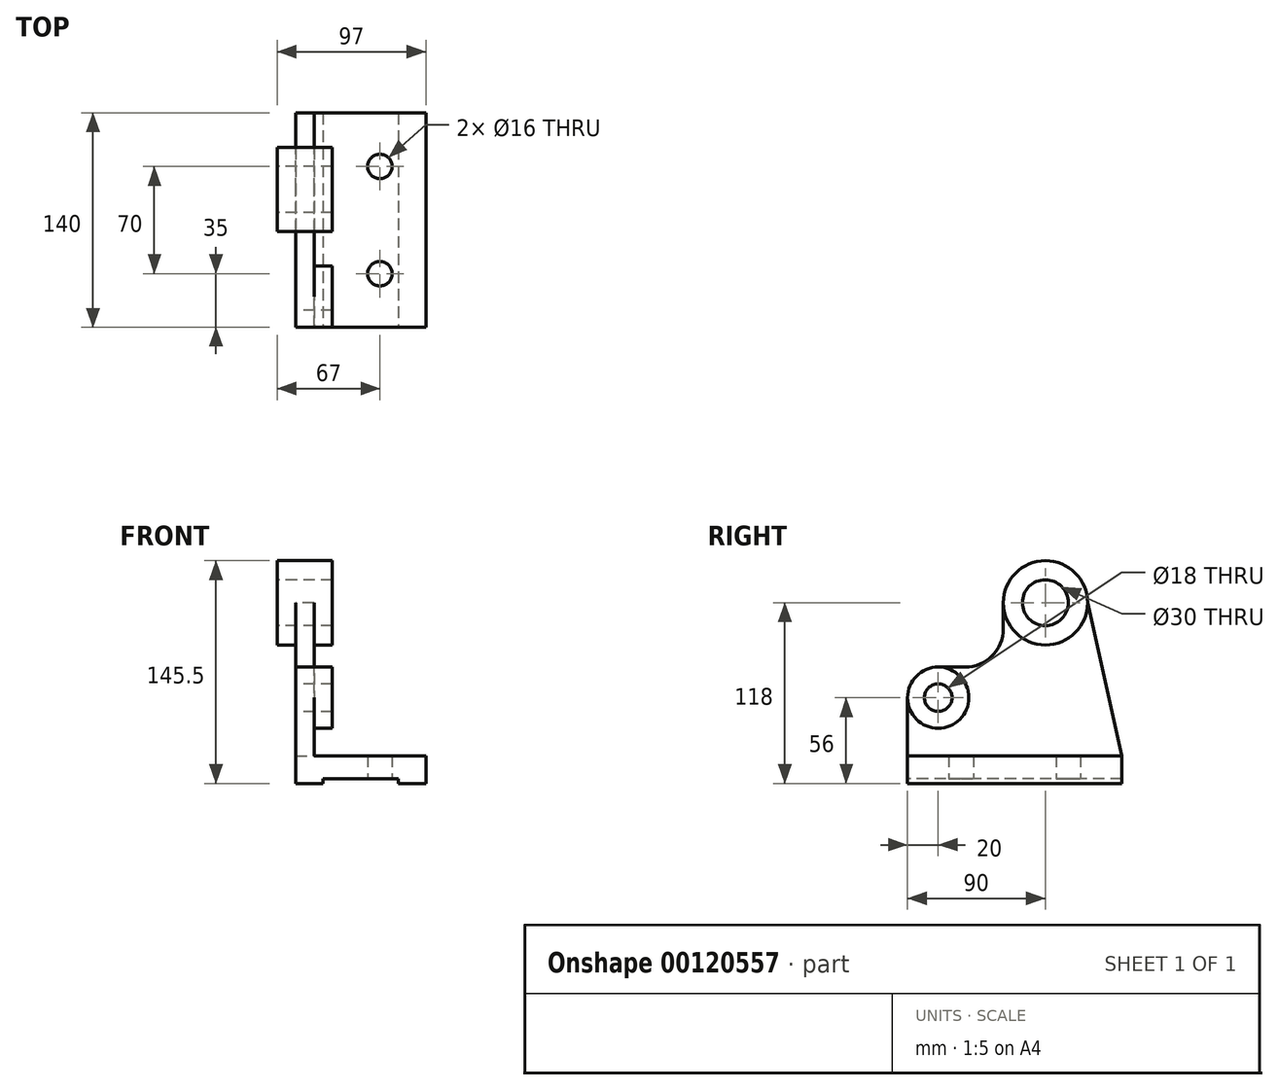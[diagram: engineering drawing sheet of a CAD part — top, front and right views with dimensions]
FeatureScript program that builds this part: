
annotation { "Feature Type Name" : "Feature", "Feature Type Description" : "" }
export const myFeature = defineFeature(function(context is Context, id is Id, definition is map)
    precondition{}
    {
        {
            var Q0;
            Q0=qCreatedBy(makeId("Top.planeOp"),FACE);
            var sketch = newSketch(context, id + "F0", { "sketchPlane" : qUnion([Q0])});
            skLineSegment(sketch, "E0.bottom", {"start": v(0, 70) * mm, "end": v(85, 70) * mm});
            skLineSegment(sketch, "E0.top", {"start": v(0, -70) * mm, "end": v(85, -70) * mm});
            skLineSegment(sketch, "E0.left", {"start": v(0, 70) * mm, "end": v(0, -70) * mm});
            skLineSegment(sketch, "E0.right", {"start": v(85, 70) * mm, "end": v(85, -70) * mm});
            skCircle(sketch, "E1", {"center": v(55, -35) * mm, "radius": 8 * mm});
            skCircle(sketch, "E2.MirrorC", {"center": v(55, 35) * mm, "radius": 8 * mm});
            skSolve(sketch);
        }
        {
            var Q0;
            Q0 = qSketchRegion(id + "F0", true);
            var Q1;
            Q1=makeQuery(id+"F0.imprint","IMPRINT",FACE,{"disambiguationData":[TD([[makeQuery(id+"F0.imprint","IMPRINT",EDGE,{"derivedFrom":sQuery(id+"F0.wireOp",EDGE,"E0.bottom")}),-1.0]])]});
            extrude(context, id + "F1", {"entities" : qUnion([Q0, Q1]), "depth" : 18 * mm});
        }
        {
            var Q0;
            Q0=makeQuery(id+"F1.opExtrude","SWEPT_FACE",FACE,{"disambiguationData":[OSD([sQuery(id+"F0.wireOp",EDGE,"E0.top")])]});
            var sketch = newSketch(context, id + "F2", { "sketchPlane" : qUnion([Q0])});
            skLineSegment(sketch, "E3", {"start": v(0, 0) * mm, "end": v(18, 0) * mm});
            skLineSegment(sketch, "E4", {"start": v(18, 0) * mm, "end": v(18, 3) * mm});
            skLineSegment(sketch, "E5", {"start": v(18, 3) * mm, "end": v(67, 3) * mm});
            skLineSegment(sketch, "E6", {"start": v(67, 3) * mm, "end": v(67, 0) * mm});
            skLineSegment(sketch, "E7", {"start": v(67, 0) * mm, "end": v(85, 0) * mm});
            skSolve(sketch);
        }
        {
            var Q0;
            Q0 = qSketchRegion(id + "F2", true);
            var Q1;
            {var subQ0=sQuery(id+"F2.wireOp",EDGE,"E4");Q1=makeQuery(id+"F2.imprint","IMPRINT",FACE,{"disambiguationData":[TD([[makeQuery(id+"F2.imprint","IMPRINT",EDGE,{"derivedFrom":subQ0}),-1.0]])]});}
            extrude(context, id + "F3", {"entities" : qUnion([Q0, Q1]), "operationType" : NewBodyOperationType.REMOVE, "endBound" : BoundingType.THROUGH_ALL, "oppositeDirection" : true, "depth" : 25 * mm});
        }
        {
            var Q0;
            Q0=makeQuery(id+"F1.opExtrude","CAP_FACE",FACE,{"disambiguationData":[OSD([sQuery(id+"F0.wireOp",EDGE,"E0.bottom"),sQuery(id+"F0.wireOp",EDGE,"E0.top"),sQuery(id+"F0.wireOp",EDGE,"E0.left"),sQuery(id+"F0.wireOp",EDGE,"E0.right")])],"isStart":false});
            var sketch = newSketch(context, id + "F4", { "sketchPlane" : qUnion([Q0])});
            skLineSegment(sketch, "E8.bottom", {"start": v(0, 70) * mm, "end": v(12, 70) * mm});
            skLineSegment(sketch, "E8.top", {"start": v(0, -70) * mm, "end": v(12, -70) * mm});
            skLineSegment(sketch, "E8.left", {"start": v(0, 70) * mm, "end": v(0, -70) * mm});
            skLineSegment(sketch, "E8.right", {"start": v(12, 70) * mm, "end": v(12, -70) * mm});
            skSolve(sketch);
        }
        {
            var Q0;
            Q0=makeQuery(id+"F4.imprint","IMPRINT",FACE,{"disambiguationData":[TD([[makeQuery(id+"F4.imprint","IMPRINT",EDGE,{"derivedFrom":sQuery(id+"F4.wireOp",EDGE,"E8.bottom")}),-1.0]])]});
            extrude(context, id + "F5", {"entities" : qUnion([Q0]), "operationType" : NewBodyOperationType.ADD, "depth" : 100 * mm});
        }
        {
            var Q0;
            Q0=makeQuery(id+"F5.opExtrude","SWEPT_FACE",FACE,{"disambiguationData":[OSD([sQuery(id+"F4.wireOp",EDGE,"E8.right")])]});
            var sketch = newSketch(context, id + "F6", { "sketchPlane" : qUnion([Q0])});
            skCircle(sketch, "E9", {"center": v(20, 118) * mm, "radius": 27.5 * mm});
            skCircle(sketch, "E10", {"center": v(20, 118) * mm, "radius": 15 * mm});
            skCircle(sketch, "E11", {"center": v(-50, 56) * mm, "radius": 20 * mm});
            skCircle(sketch, "E12", {"center": v(-50, 56) * mm, "radius": 9 * mm});
            skLineSegment(sketch, "E13", {"start": v(-50, 76) * mm, "end": v(-7.5, 76) * mm});
            skLineSegment(sketch, "E14", {"start": v(20, 118) * mm, "end": v(-7.5, 118) * mm});
            skLineSegment(sketch, "E15", {"start": v(-7.5, 118) * mm, "end": v(-7.5, 76) * mm});
            skLineSegment(sketch, "E16", {"start": v(47.5, 118) * mm, "end": v(70, 18) * mm});
            skSolve(sketch);
        }
        {
            var Q0;
            Q0=makeQuery(id+"F6.imprint","IMPRINT",FACE,{"disambiguationData":[TD([[makeQuery(id+"F6.imprint","IMPRINT",EDGE,{"derivedFrom":sQuery(id+"F6.wireOp",EDGE,"E11")}),1.0]])]});
            extrude(context, id + "F7", {"entities" : qUnion([Q0]), "operationType" : NewBodyOperationType.ADD, "depth" : 12 * mm});
        }
        {
            var Q0;
            Q0=qCreatedBy(makeId("Right.planeOp"),FACE);
            cPlane(context, id + "F8", {"entities" : qUnion([Q0]), "cplaneType" : CPlaneType.OFFSET, "offset" : 6 * mm, "width" : 150 * mm, "height" : 150 * mm});
        }
        {
            var Q0;
            Q0=qCreatedBy(id+"F8.planeOp",FACE);
            var sketch = newSketch(context, id + "F9", { "sketchPlane" : qUnion([Q0])});
            skCircle(sketch, "E17", {"center": v(20, 118) * mm, "radius": 15 * mm});
            skCircle(sketch, "E18", {"center": v(20, 118) * mm, "radius": 27.5 * mm});
            skSolve(sketch);
        }
        {
            var Q0;
            Q0=makeQuery(id+"F9.imprint","IMPRINT",FACE,{"disambiguationData":[TD([[makeQuery(id+"F9.imprint","IMPRINT",EDGE,{"derivedFrom":sQuery(id+"F9.wireOp",EDGE,"E17")}),-1.0]])]});
            extrude(context, id + "F10", {"entities" : qUnion([Q0]), "operationType" : NewBodyOperationType.ADD, "endBound" : BoundingType.SYMMETRIC, "depth" : 36 * mm});
        }
        {
            var Q0;
            Q0=makeQuery(id+"F6.imprint","IMPRINT",FACE,{"disambiguationData":[TD([[makeQuery(id+"F6.imprint","IMPRINT",EDGE,{"derivedFrom":sQuery(id+"F6.wireOp",EDGE,"E12")}),1.0]])]});
            var Q1;
            {var subQ0=sQuery(id+"F6.wireOp",EDGE,"E10");var subQ1=makeQuery(id+"F5.opExtrude","CAP_EDGE",EDGE,{"disambiguationData":[OSD([sQuery(id+"F4.wireOp",EDGE,"E8.right")])],"isStart":false});var subQ2=makeQuery(id+"F6.imprint","INTERSECT",VERTEX,{"disambiguationData":[OD(0.0)],"derivedFrom":[subQ1,subQ0]});Q1=makeQuery(id+"F6.imprint","IMPRINT",FACE,{"disambiguationData":[TD([[makeQuery(id+"F6.imprint","IMPRINT",EDGE,{"disambiguationData":[TD([[subQ2,1.0]])],"derivedFrom":subQ0}),1.0]])]});}
            extrude(context, id + "F11", {"entities" : qUnion([Q0, Q1]), "operationType" : NewBodyOperationType.REMOVE, "oppositeDirection" : true, "depth" : 25 * mm});
        }
        {
            var Q0;
            {var subQ0=sQuery(id+"F6.wireOp",EDGE,"E13");Q0=makeQuery(id+"F6.imprint","IMPRINT",FACE,{"disambiguationData":[TD([[makeQuery(id+"F6.imprint","IMPRINT",EDGE,{"derivedFrom":subQ0}),1.0]])]});}
            var Q1;
            {var subQ0=sQuery(id+"F6.wireOp",EDGE,"E16");Q1=makeQuery(id+"F6.imprint","IMPRINT",FACE,{"disambiguationData":[TD([[makeQuery(id+"F6.imprint","IMPRINT",EDGE,{"derivedFrom":subQ0}),1.0]])]});}
            extrude(context, id + "F12", {"entities" : qUnion([Q0, Q1]), "operationType" : NewBodyOperationType.REMOVE, "oppositeDirection" : true, "depth" : 25 * mm});
        }
        {
            var Q0;
            Q0=makeQuery(id+"F12.boolean.opBoolean","COPY",EDGE,{"derivedFrom":makeQuery(id+"F12.opExtrude","SWEPT_EDGE",EDGE,{"disambiguationData":[OSD([sQuery(id+"F6.wireOp",EDGE,"E13"),sQuery(id+"F6.wireOp",EDGE,"E15")])]})});
            fillet(context, id + "F13", {"entities" : qUnion([Q0]), "radius" : 25 * mm, "tangentPropagation" : true, "allowEdgeOverflow" : false});
        }
        {
            var Q0;
            Q0=makeQuery(id+"F0.imprint","IMPRINT",FACE,{"disambiguationData":[TD([[makeQuery(id+"F0.imprint","IMPRINT",EDGE,{"derivedFrom":sQuery(id+"F0.wireOp",EDGE,"E1")}),1.0]])]});
            var Q1;
            Q1=makeQuery(id+"F0.imprint","IMPRINT",FACE,{"disambiguationData":[TD([[makeQuery(id+"F0.imprint","IMPRINT",EDGE,{"derivedFrom":sQuery(id+"F0.wireOp",EDGE,"E2.MirrorC")}),-1.0]])]});
            extrude(context, id + "F14", {"entities" : qUnion([Q0, Q1]), "operationType" : NewBodyOperationType.REMOVE, "oppositeDirection" : true, "depth" : 25 * mm});
        }
    });
